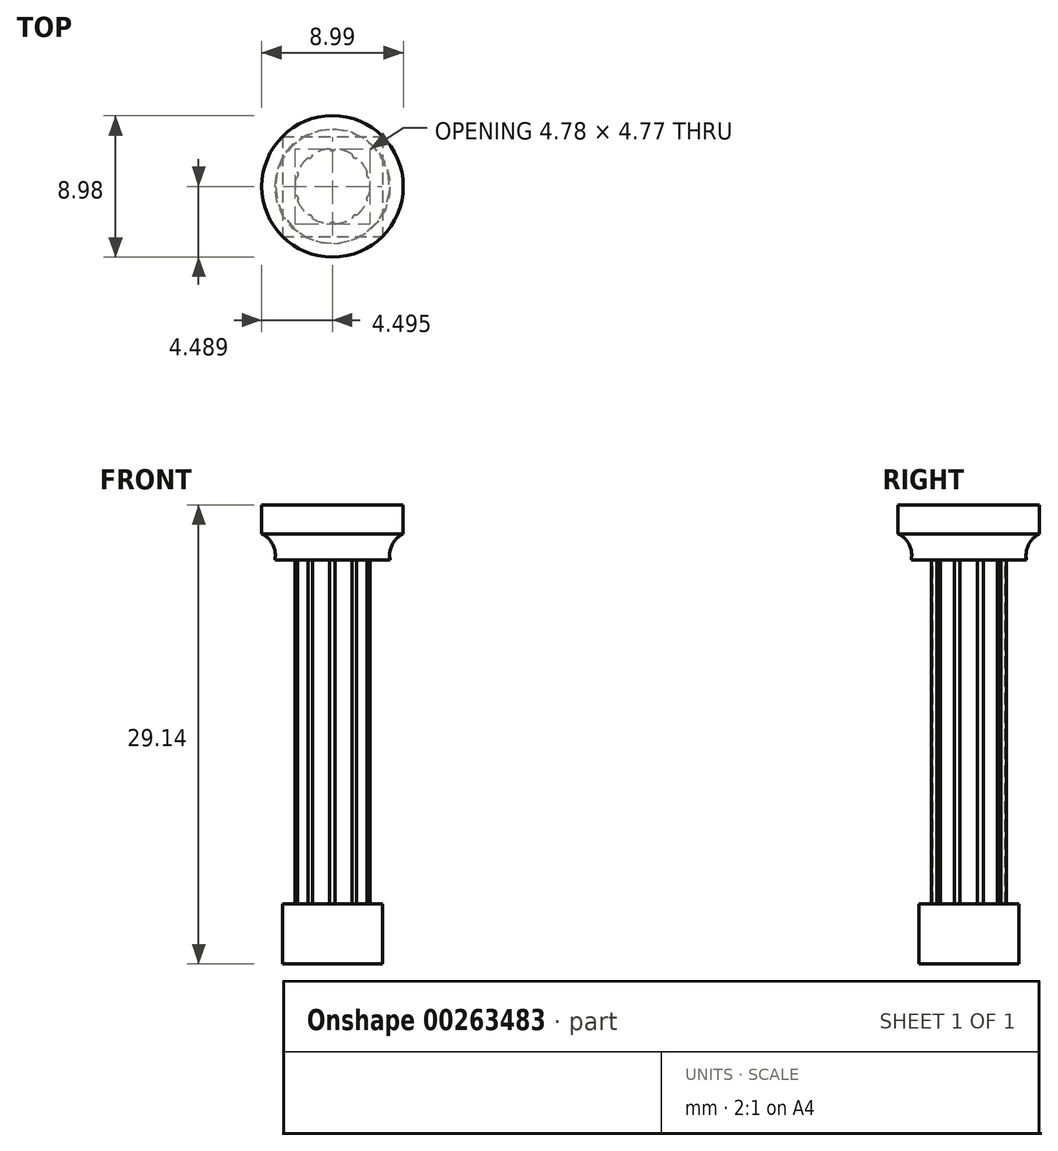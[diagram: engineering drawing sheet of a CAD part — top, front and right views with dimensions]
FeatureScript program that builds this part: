
annotation { "Feature Type Name" : "Feature", "Feature Type Description" : "" }
export const myFeature = defineFeature(function(context is Context, id is Id, definition is map)
    precondition{}
    {
        {
            var Q0;
            Q0=qCreatedBy(makeId("Top.planeOp"),FACE);
            var sketch = newSketch(context, id + "F0", { "sketchPlane" : qUnion([Q0])});
            skLineSegment(sketch, "E0.bottom", {"start": v(-0.63, -7.69) * mm, "end": v(5.72, -7.69) * mm});
            skLineSegment(sketch, "E0.top", {"start": v(-0.63, -14.04) * mm, "end": v(5.72, -14.04) * mm});
            skLineSegment(sketch, "E0.left", {"start": v(-0.63, -7.69) * mm, "end": v(-0.63, -14.04) * mm});
            skLineSegment(sketch, "E0.right", {"start": v(5.72, -7.69) * mm, "end": v(5.72, -14.04) * mm});
            skSolve(sketch);
        }
        {
            var Q0;
            Q0 = qSketchRegion(id + "F0", true);
            extrude(context, id + "F1", {"entities" : qUnion([Q0]), "depth" : 3.8 * mm});
        }
        {
            var Q0;
            Q0=makeQuery(id+"F1.opExtrude","CAP_FACE",FACE,{"disambiguationData":[OSD([sQuery(id+"F0.wireOp",EDGE,"E0.bottom"),sQuery(id+"F0.wireOp",EDGE,"E0.top"),sQuery(id+"F0.wireOp",EDGE,"E0.left"),sQuery(id+"F0.wireOp",EDGE,"E0.right")])],"isStart":false});
            var sketch = newSketch(context, id + "F2", { "sketchPlane" : qUnion([Q0])});
            skCircle(sketch, "E1", {"center": v(2.54, -10.86) * mm, "radius": 2.39 * mm});
            skPoint(sketch, "E1.centerSnap0", {"position": v(2.54, -7.69) * mm});
            skPoint(sketch, "E1.centerSnap1", {"position": v(-0.63, -10.86) * mm});
            skSolve(sketch);
        }
        {
            var Q0;
            Q0 = qSketchRegion(id + "F2", true);
            extrude(context, id + "F3", {"entities" : qUnion([Q0]), "operationType" : NewBodyOperationType.ADD, "depth" : 25.4 * mm});
        }
        {
            var Q0;
            Q0=makeQuery(id+"F1.opExtrude","SWEPT_BODY",BODY,{"disambiguationData":[OSD([sQuery(id+"F0.wireOp",EDGE,"E0.bottom"),sQuery(id+"F0.wireOp",EDGE,"E0.top"),sQuery(id+"F0.wireOp",EDGE,"E0.left"),sQuery(id+"F0.wireOp",EDGE,"E0.right")])]});
            transform(context, id + "F4", {"entities" : qUnion([Q0]), "transformType" : TransformType.TRANSLATION_3D, "dx" : -2.5 * mm, "dy" : 10.82 * mm, "dz" : 0 * mm, "makeCopy" : false});
        }
        {
            var Q0;
            Q0=qCreatedBy(makeId("Front.planeOp"),FACE);
            var sketch = newSketch(context, id + "F5", { "sketchPlane" : qUnion([Q0])});
            skLineSegment(sketch, "E2.bottom", {"start": v(2.4, 29.14) * mm, "end": v(3.72, 29.14) * mm});
            skLineSegment(sketch, "E2.top", {"start": v(2.4, 25.66) * mm, "end": v(3.72, 25.66) * mm});
            skLineSegment(sketch, "E2.left", {"start": v(2.4, 29.14) * mm, "end": v(2.4, 25.66) * mm});
            skLineSegment(sketch, "E3.bottom", {"start": v(3.72, 29.14) * mm, "end": v(4.55, 29.14) * mm});
            skLineSegment(sketch, "E3.right", {"start": v(4.55, 29.14) * mm, "end": v(4.55, 27.3) * mm});
            skArc(sketch, "E4", {"start": v(4.55, 27.3) * mm, "mid": v(3.85, 26.63) * mm, "end": v(3.72, 25.66) * mm});
            skSolve(sketch);
        }
        {
            var Q0;
            Q0 = qSketchRegion(id + "F5", true);
            var Q1;
            Q1=makeQuery(id+"F3.opExtrude","CAP_EDGE",EDGE,{"disambiguationData":[OSD([sQuery(id+"F2.wireOp",EDGE,"E1")])],"isStart":false});
            revolve(context, id + "F6", {"operationType" : NewBodyOperationType.ADD, "entities" : qUnion([Q0]), "axis" : qUnion([Q1]), "revolveType" : RevolveType.FULL});
        }
        {
            var Q0;
            Q0=makeQuery(id+"F1.opExtrude","SWEPT_BODY",BODY,{"disambiguationData":[OSD([sQuery(id+"F0.wireOp",EDGE,"E0.bottom"),sQuery(id+"F0.wireOp",EDGE,"E0.top"),sQuery(id+"F0.wireOp",EDGE,"E0.left"),sQuery(id+"F0.wireOp",EDGE,"E0.right")])]});
            transform(context, id + "F7", {"entities" : qUnion([Q0]), "transformType" : TransformType.TRANSLATION_3D, "dx" : -0.05 * mm, "dy" : 0.05 * mm, "dz" : 0 * mm, "makeCopy" : false});
        }
        {
            var Q0;
            Q0=makeQuery(id+"F3.opExtrude","CAP_FACE",FACE,{"disambiguationData":[OSD([sQuery(id+"F2.wireOp",EDGE,"E1")])],"isStart":false});
            var sketch = newSketch(context, id + "F8", { "sketchPlane" : qUnion([Q0])});
            skArc(sketch, "E5", {"start": v(-0.2, 2.4) * mm, "mid": v(0, 2.29) * mm, "end": v(0.19, 2.4) * mm});
            skCircle(sketch, "E6", {"center": v(0, 2.5) * mm, "radius": 0.22 * mm});
            skCircle(sketch, "E7.1.0", {"center": v(-1.48, 2.03) * mm, "radius": 0.22 * mm});
            skCircle(sketch, "E7.2.0", {"center": v(-2.39, 0.77) * mm, "radius": 0.22 * mm});
            skCircle(sketch, "E7.3.0", {"center": v(-2.38, -0.78) * mm, "radius": 0.22 * mm});
            skCircle(sketch, "E7.4.0", {"center": v(-1.47, -2.03) * mm, "radius": 0.22 * mm});
            skCircle(sketch, "E7.5.0", {"center": v(0, -2.5) * mm, "radius": 0.22 * mm});
            skCircle(sketch, "E7.6.0", {"center": v(1.48, -2.03) * mm, "radius": 0.22 * mm});
            skCircle(sketch, "E7.7.0", {"center": v(2.39, -0.77) * mm, "radius": 0.22 * mm});
            skCircle(sketch, "E7.8.0", {"center": v(2.38, 0.78) * mm, "radius": 0.22 * mm});
            skCircle(sketch, "E7.9.0", {"center": v(1.47, 2.03) * mm, "radius": 0.22 * mm});
            skPoint(sketch, "E7.center", {"position": v(0, 0) * mm});
            skSolve(sketch);
        }
        {
            var Q0;
            Q0 = qSketchRegion(id + "F8", true);
            extrude(context, id + "F9", {"entities" : qUnion([Q0]), "operationType" : NewBodyOperationType.REMOVE, "oppositeDirection" : true, "depth" : 25.4 * mm});
        }
        {
            var Q0;
            Q0=makeQuery(id+"F6.opRevolve","SWEPT_FACE",FACE,{"disambiguationData":[OSD([sQuery(id+"F5.wireOp",EDGE,"E2.bottom"),sQuery(id+"F5.wireOp",EDGE,"E3.bottom")])]});
            var sketch = newSketch(context, id + "F10", { "sketchPlane" : qUnion([Q0])});
            skCircle(sketch, "E8", {"center": v(0, 0) * mm, "radius": 2.73 * mm});
            skSolve(sketch);
        }
        {
            var Q0;
            Q0 = qSketchRegion(id + "F10", true);
            extrude(context, id + "F11", {"entities" : qUnion([Q0]), "operationType" : NewBodyOperationType.ADD, "oppositeDirection" : true, "depth" : 3.48 * mm});
        }
        {
            var Q0;
            Q0=makeQuery(id+"F11.boolean.opBoolean","MERGE",FACE,{"derivedFrom":[makeQuery(id+"F6.opRevolve","SWEPT_FACE",FACE,{"disambiguationData":[OSD([sQuery(id+"F5.wireOp",EDGE,"E2.bottom"),sQuery(id+"F5.wireOp",EDGE,"E3.bottom")])]}),makeQuery(id+"F11.opExtrude","CAP_FACE",FACE,{"disambiguationData":[OSD([sQuery(id+"F10.wireOp",EDGE,"E8")])],"isStart":true})]});
            var sketch = newSketch(context, id + "F12", { "sketchPlane" : qUnion([Q0])});
            skLineSegment(sketch, "E9.bottom", {"start": v(-2.9, 3.17) * mm, "end": v(2.91, 3.17) * mm});
            skLineSegment(sketch, "E9.top", {"start": v(-2.9, -2.92) * mm, "end": v(2.91, -2.92) * mm});
            skLineSegment(sketch, "E9.left", {"start": v(-2.9, 3.17) * mm, "end": v(-2.9, -2.92) * mm});
            skLineSegment(sketch, "E9.right", {"start": v(2.91, 3.17) * mm, "end": v(2.91, -2.92) * mm});
            skSolve(sketch);
        }
        {
            var Q0;
            Q0 = qSketchRegion(id + "F12", true);
            extrude(context, id + "F13", {"entities" : qUnion([Q0]), "operationType" : NewBodyOperationType.REMOVE, "depth" : 25.4 * mm});
        }
    });
